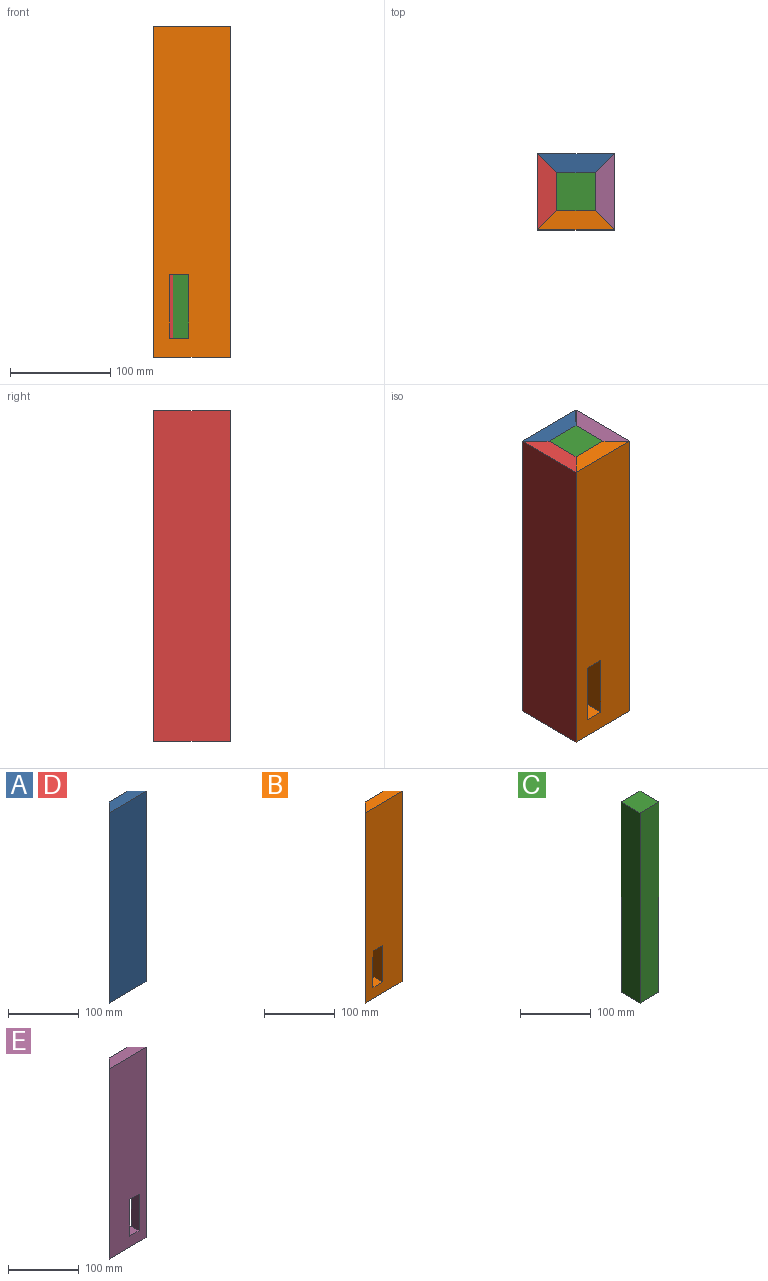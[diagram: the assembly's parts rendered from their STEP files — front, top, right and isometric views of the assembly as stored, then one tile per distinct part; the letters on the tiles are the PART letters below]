
ASSEMBLY  parts=5 mates=4
PART A: 6 faces, bbox 76.2x19.1x330.2 mm
  f0: plane 330.2x19.05mm, normal (0.71,0.71,0), area 8895.8mm2, adj f1,f2,f3,f4
  f1: plane 330.2x76.2mm, normal (0,-1,0), area 25161.2mm2, adj f0,f2,f4,f5
  f2: plane 76.2x19.05mm, normal (0,0,-1), area 1088.7mm2, adj f0,f1,f3,f5
  f3: plane 330.2x38.1mm, normal (0,1,0), area 12580.6mm2, adj f0,f2,f4,f5
  f4: plane 76.2x19.05mm, normal (0,0,1), area 1088.7mm2, adj f0,f1,f3,f5
  f5: plane 330.2x19.05mm, normal (-0.71,0.71,0), area 8895.8mm2, adj f1,f2,f3,f4
PART B: 10 faces, bbox 76.2x19.1x330.2 mm
  f0: plane 63.5x15.88mm, normal (1,0,0), area 1008.1mm2, adj f4,f5,f6,f7
  f1: plane 76.2x19.05mm, normal (0,0,1), area 1088.7mm2, adj f2,f4,f6,f8
  f2: plane 330.2x19.05mm, normal (0.71,0.71,0), area 8895.8mm2, adj f1,f3,f6,f8
  f3: plane 76.2x19.05mm, normal (0,0,-1), area 1088.7mm2, adj f2,f4,f6,f8
  f4: plane 330.2x19.05mm, normal (-0.71,0.71,0), area 8610.7mm2, adj f0,f1,f3,f5,f6,f7,f8
  f5: plane 19.05x19.05mm, normal (0,0,-1), area 357.9mm2, adj f0,f4,f6,f8,f9
  f6: plane 330.2x76.2mm, normal (0,-1,0), area 23951.6mm2, adj f0,f1,f2,f3,f4,f5,f7,f9
  f7: plane 19.05x19.05mm, normal (0,0,1), area 357.9mm2, adj f0,f4,f6,f8,f9
  f8: plane 330.2x38.1mm, normal (0,1,0), area 11572.6mm2, adj f1,f2,f3,f4,f5,f7,f9
  f9: plane 63.5x19.05mm, normal (-1,0,0), area 1209.7mm2, adj f5,f6,f7,f8
PART C: 6 faces, bbox 38.1x38.1x330.2 mm
  f0: plane 330.2x38.1mm, normal (-1,0,0), area 12580.6mm2, adj f1,f2,f3,f4
  f1: plane 38.1x38.1mm, normal (0,0,-1), area 1451.6mm2, adj f0,f2,f4,f5
  f2: plane 330.2x38.1mm, normal (0,1,0), area 12580.6mm2, adj f0,f1,f3,f5
  f3: plane 38.1x38.1mm, normal (0,0,1), area 1451.6mm2, adj f0,f2,f4,f5
  f4: plane 330.2x38.1mm, normal (0,-1,0), area 12580.6mm2, adj f0,f1,f3,f5
  f5: plane 330.2x38.1mm, normal (1,0,0), area 12580.6mm2, adj f1,f2,f3,f4
PART D: same geometry as A
PART E: 10 faces, bbox 76.2x19.1x330.2 mm
  f0: plane 63.5x15.88mm, normal (-1,0,0), area 1008.1mm2, adj f4,f5,f6,f7
  f1: plane 76.2x19.05mm, normal (0,0,-1), area 1088.7mm2, adj f2,f4,f6,f8
  f2: plane 330.2x19.05mm, normal (-0.71,0.71,0), area 8895.8mm2, adj f1,f3,f6,f8
  f3: plane 76.2x19.05mm, normal (0,0,1), area 1088.7mm2, adj f2,f4,f6,f8
  f4: plane 330.2x19.05mm, normal (0.71,0.71,0), area 8610.7mm2, adj f0,f1,f3,f5,f6,f7,f8
  f5: plane 19.05x19.05mm, normal (0,0,1), area 357.9mm2, adj f0,f4,f6,f8,f9
  f6: plane 330.2x76.2mm, normal (0,-1,0), area 23951.6mm2, adj f0,f1,f2,f3,f4,f5,f7,f9
  f7: plane 19.05x19.05mm, normal (0,0,-1), area 357.9mm2, adj f0,f4,f6,f8,f9
  f8: plane 330.2x38.1mm, normal (0,1,0), area 11572.6mm2, adj f1,f2,f3,f4,f5,f7,f9
  f9: plane 63.5x19.05mm, normal (1,0,0), area 1209.7mm2, adj f5,f6,f7,f8
PLACE A rot(axis=(0,0,1),180deg) t=(-19.12,90.35,-8.61)mm
PLACE B t=(-95.32,52.25,-8.61)mm
PLACE C t=(-76.27,90.35,-8.61)mm fixed
PLACE D rot(axis=(0,0,-1),90deg) t=(-76.27,109.4,-8.61)mm
PLACE E rot(axis=(0,0,1),90deg) t=(-38.17,33.2,-8.61)mm
MATE fastened A.f2 <-> D.f2  axis (0,0,-1) through (-95.32,109.4,-8.61)mm
MATE fastened E.f1 <-> B.f3  axis (0,0,-1) through (-19.12,33.2,-8.61)mm
MATE fastened D.f2 <-> B.f3  axis (0,0,-1) through (-95.32,33.2,-8.61)mm
MATE fastened C.f1 <-> D.f2  axis (0,0,-1) through (-76.27,52.25,-8.61)mm
